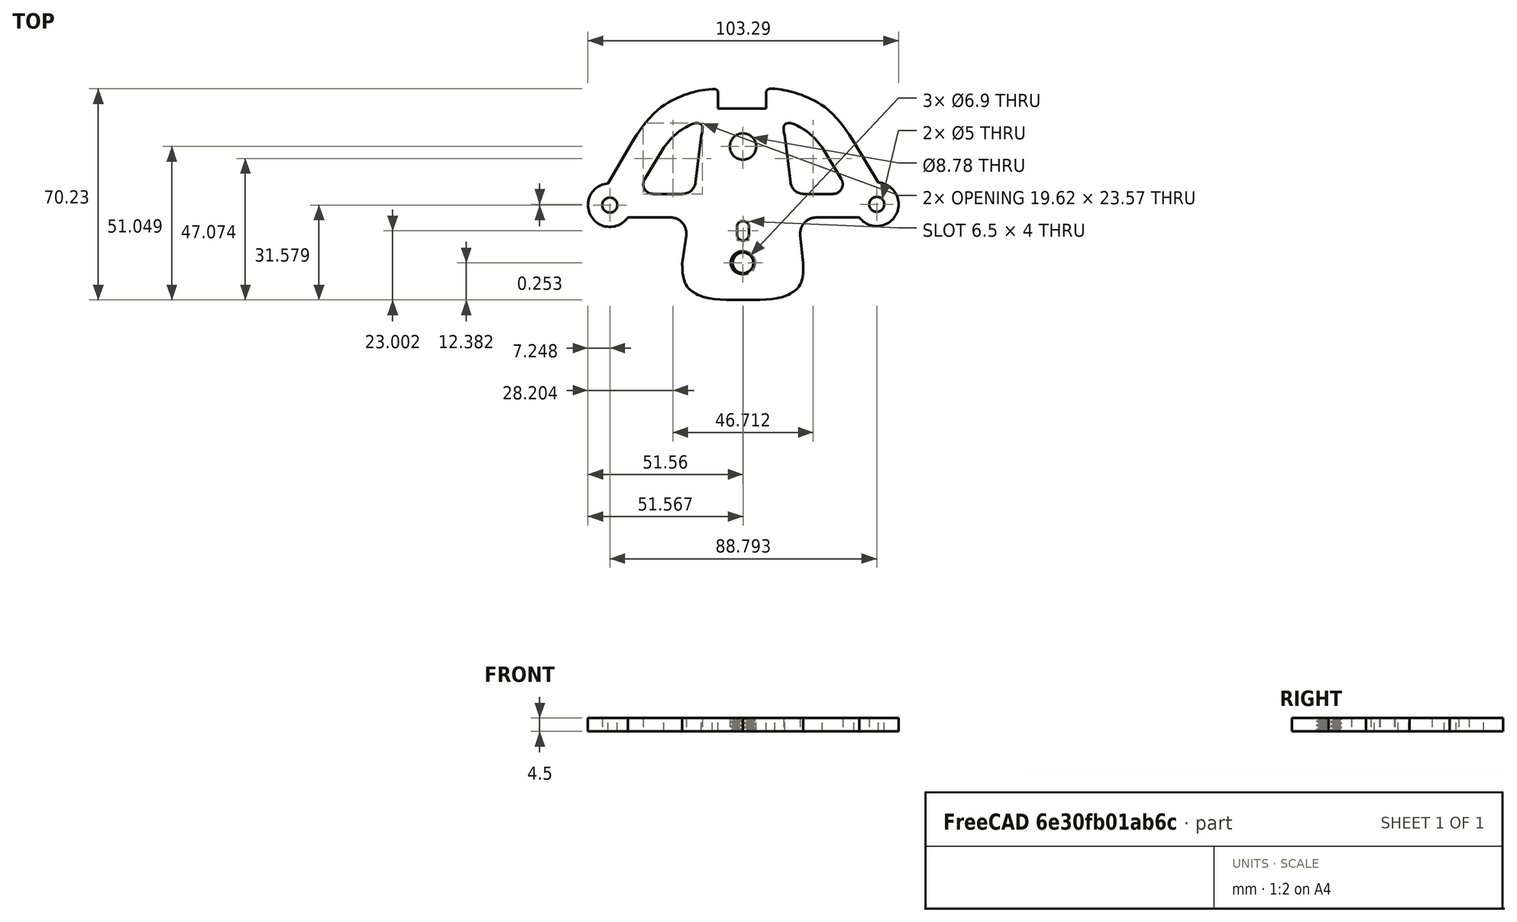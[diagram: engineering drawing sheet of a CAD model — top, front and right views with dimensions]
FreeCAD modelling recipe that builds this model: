
FCSTD DOCUMENT  (FreeCAD 0.20R29603 (Git))
Label: tiller-plate-final-drawing
License: Creative Commons Attribution
LicenseURL: http://creativecommons.org/licenses/by/4.0/
objects: TechDraw::DrawViewDimension×10, TechDraw::DrawRichAnno×4, TechDraw::DrawProjGroupItem×3, Sketcher::SketchObject×2, TechDraw::DrawLeaderLine×2, Image::ImagePlane×1, PartDesign::Pad×1, PartDesign::Hole×1, PartDesign::Body×1, Part::Refine×1, Mesh::Feature×1, TechDraw::DrawSVGTemplate×1, TechDraw::DrawViewPart×1, TechDraw::DrawViewAnnotation×1, TechDraw::DrawProjGroup×1, TechDraw::DrawGeomHatch×1, TechDraw::DrawPage×1
note: 8 computed .brp shape members not serialized (recipe doc carries the construction recipe); baked Part::Feature solids carry a one-line shape summary decoded from their .brp

FEATURE [Image::ImagePlane] ImagePlane
  Placement = pos=(0.718471,-0.887185,-0.1) rot=(0,0,-1;6.26573rad)
  XSize = 116.42
  YSize = 72.9857
FEATURE [Sketcher::SketchObject] Sketch
  FullyConstrained = false
  MapMode = 5
  Support = -> [XY_Plane]
  sketch-geometry (75):
    g0: ArcOfCircle CenterX=-44.3115 CenterY=-4.63128 CenterZ=0 NormalX=0 NormalY=0 NormalZ=1 AngleXU=0 Radius=7.25 StartAngle=1.65486 EndAngle=5.682
    g1: LineSegment StartX=-8.31257 StartY=27.4789 StartZ=0 EndX=7.68743 EndY=27.4789 EndZ=0
    g2: ArcOfCircle CenterX=44.4815 CenterY=-4.37835 CenterZ=0 NormalX=0 NormalY=0 NormalZ=1 AngleXU=0 Radius=7.25 StartAngle=3.79043 EndAngle=7.77353
    g3-g7: Circle x5 (B-spline internal-alignment scaffolding for g8; pole/knot coordinates omitted)
    g8: BSplineCurve PolesCount=5 KnotsCount=3 Degree=3 IsPeriodic=0
    g9: GeomPoint X=-36.8504 Y=16.2655 Z=0
    g10: GeomPoint X=-22.0365 Y=30.9294 Z=0
    g11: GeomPoint X=-10.281 Y=33.9118 Z=0
    g12: LineSegment StartX=-8.31257 StartY=27.4789 StartZ=0 EndX=-8.31257 EndY=32.8031 EndZ=0
    g13: LineSegment StartX=-10.281 StartY=33.9118 StartZ=0 EndX=-9.42128 EndY=33.9118 EndZ=0
    g14: ArcOfCircle CenterX=-9.42128 CenterY=32.8031 CenterZ=0 NormalX=0 NormalY=0 NormalZ=1 AngleXU=0 Radius=1.10871 StartAngle=2.2e-15 EndAngle=1.5708
    g15: LineSegment StartX=-44.9203 StartY=2.59312 StartZ=0 EndX=-36.8504 EndY=16.2655 EndZ=0
    g16: LineSegment StartX=45.0641 StartY=2.84821 StartZ=0 EndX=36.8504 EndY=16.2655 EndZ=0
    g17: BSplineCurve PolesCount=5 KnotsCount=3 Degree=3 IsPeriodic=0
    g18: Circle CenterX=10.5661 CenterY=34.0159 CenterZ=0 NormalX=0 NormalY=0 NormalZ=1 AngleXU=0 Radius=1
    g19: GeomPoint X=10.5661 Y=34.0159 Z=0
    g20: LineSegment StartX=7.68743 StartY=27.4789 StartZ=0 EndX=7.68743 EndY=32.7328 EndZ=0
    g21: LineSegment StartX=10.5661 StartY=34.0159 StartZ=0 EndX=8.9705 EndY=34.0159 EndZ=0
    g22: ArcOfCircle CenterX=8.9705 CenterY=32.7328 CenterZ=0 NormalX=0 NormalY=0 NormalZ=1 AngleXU=0 Radius=1.28307 StartAngle=1.5708 EndAngle=3.14159
    g23: Circle CenterX=0 CenterY=14.839 CenterZ=0 NormalX=0 NormalY=0 NormalZ=1 AngleXU=0 Radius=4.39
    g24: Circle CenterX=-44.3115 CenterY=-4.63128 CenterZ=0 NormalX=0 NormalY=0 NormalZ=1 AngleXU=0 Radius=2.5
    g25: Circle CenterX=44.4815 CenterY=-4.37835 CenterZ=0 NormalX=0 NormalY=0 NormalZ=1 AngleXU=0 Radius=2.5
    g26: Circle CenterX=0 CenterY=-23.8283 CenterZ=0 NormalX=0 NormalY=0 NormalZ=1 AngleXU=0 Radius=3.375
    g27: LineSegment StartX=-24.1418 StartY=-8.73204 StartZ=0 EndX=-38.3327 EndY=-8.73204 EndZ=0
    g28: LineSegment StartX=-18.8831 StartY=-14.7976 StartZ=0 EndX=-20.2109 EndY=-24.0676 EndZ=0
    g29: ArcOfCircle CenterX=-24.1418 CenterY=-14.0444 CenterZ=0 NormalX=0 NormalY=0 NormalZ=1 AngleXU=0 Radius=5.31234 StartAngle=6.14092 EndAngle=7.85398
    g30: LineSegment StartX=24.3717 StartY=-8.75921 StartZ=0 EndX=38.7048 EndY=-8.75921 EndZ=0
    g31: ArcOfCircle CenterX=24.3717 CenterY=-14.1062 CenterZ=0 NormalX=0 NormalY=0 NormalZ=1 AngleXU=0 Radius=5.34701 StartAngle=1.5708 EndAngle=3.24394
    g32: LineSegment StartX=19.0527 StartY=-14.6525 StartZ=0 EndX=20.0104 EndY=-23.9781 EndZ=0
    g33: LineSegment StartX=-1.99308 StartY=-11.9579 StartZ=0 EndX=-1.99308 EndY=-14.4579 EndZ=0
    g34: ArcOfCircle CenterX=0.00691514 CenterY=-14.4579 CenterZ=0 NormalX=0 NormalY=0 NormalZ=1 AngleXU=0 Radius=2 StartAngle=3.14159 EndAngle=6.28319
    g35: LineSegment StartX=2.00692 StartY=-14.4579 StartZ=0 EndX=2.00692 EndY=-11.9579 EndZ=0
    g36: ArcOfCircle CenterX=0.00691514 CenterY=-11.9579 CenterZ=0 NormalX=0 NormalY=0 NormalZ=1 AngleXU=0 Radius=2 StartAngle=0 EndAngle=3.14159
    g37-g41: Circle x5 (B-spline internal-alignment scaffolding for g42; pole/knot coordinates omitted)
    g42: BSplineCurve PolesCount=5 KnotsCount=3 Degree=3 IsPeriodic=0
    g43: GeomPoint X=-20.2109 Y=-24.0676 Z=0
    g44: GeomPoint X=-16.4959 Y=-33.6189 Z=0
    g45: GeomPoint X=0 Y=-36.2033 Z=0
    g46: BSplineCurve PolesCount=5 KnotsCount=3 Degree=3 IsPeriodic=0
    g47: LineSegment StartX=-13.8688 StartY=18.3787 StartZ=0 EndX=-15.7977 EndY=2.95357 EndZ=0
    g48: LineSegment StartX=-29.9555 StartY=-0.921458 StartZ=0 EndX=-20.1874 EndY=-0.921458 EndZ=0
    g49: ArcOfCircle CenterX=-20.1874 CenterY=3.50249 CenterZ=0 NormalX=0 NormalY=0 NormalZ=1 AngleXU=0 Radius=4.42394 StartAngle=4.71239 EndAngle=6.15879
    g50: LineSegment StartX=-26.3153 StartY=14.4759 StartZ=0 EndX=-32.7012 EndY=3.9578 EndZ=0
    g51: ArcOfCircle CenterX=-29.9555 CenterY=2.29074 CenterZ=0 NormalX=0 NormalY=0 NormalZ=1 AngleXU=0 Radius=3.2122 StartAngle=2.59594 EndAngle=4.71239
    g52-g57: Circle x6 (B-spline internal-alignment scaffolding for g58; pole/knot coordinates omitted)
    g58: BSplineCurve PolesCount=6 KnotsCount=4 Degree=3 IsPeriodic=0
    g59-g62: GeomPoint x4 (B-spline internal-alignment scaffolding for g58; pole/knot coordinates omitted)
    g63: GeomPoint X=0 Y=-23.8283 Z=0
    g64: LineSegment StartX=26.3153 StartY=14.4759 StartZ=0 EndX=32.7012 EndY=3.9578 EndZ=0
    g65: BSplineCurve PolesCount=6 KnotsCount=4 Degree=3 IsPeriodic=0
    g66: LineSegment StartX=13.8688 StartY=18.3787 StartZ=0 EndX=15.7977 EndY=2.95357 EndZ=0
    g67: ArcOfCircle CenterX=20.1874 CenterY=3.50249 CenterZ=0 NormalX=0 NormalY=0 NormalZ=1 AngleXU=0 Radius=4.42394 StartAngle=3.26599 EndAngle=4.71239
    g68: LineSegment StartX=29.9555 StartY=-0.921458 StartZ=0 EndX=20.1874 EndY=-0.921458 EndZ=0
    g69: ArcOfCircle CenterX=29.9555 CenterY=2.29074 CenterZ=0 NormalX=0 NormalY=0 NormalZ=1 AngleXU=0 Radius=3.2122 StartAngle=4.71239 EndAngle=6.82884
    g70: GeomPoint X=-0.103427 Y=-16.4548 Z=0
    g71: GeomPoint X=-0.101997 Y=-20.4548 Z=0
    g72: GeomPoint X=0.0131789 Y=-27.2033 Z=0
    g73: GeomPoint X=-0.00257 Y=27.4789 Z=0
    g74: GeomPoint X=-0.0300529 Y=19.2289 Z=0
  constraints (86):
    c: Radius(g0) = 7.25
    c: Horizontal(g1)
    c: Equal(g2,g0)
    c: Equal(g3, g4-g7) x4
    c: InternalAlignment(g3-g7 -> g8) x5
    c: InternalAlignment(g9,g8)
    c: InternalAlignment(g10,g8)
    c: InternalAlignment(g11,g8)
    c: Coincident(g12,g1)
    c: Coincident(g13,g8)
    c: Horizontal(g13)
    c: Tangent(g12,g14) = -1.5708
    c: Tangent(g13,g14) = 1.5708
    c: Coincident(g15,g8)
    c: InternalAlignment(g18,g17)
    c: InternalAlignment(g19,g17)
    c: Coincident(g21,g17)
    c: Horizontal(g21)
    c: Tangent(g20,g22) = 1.5708
    c: Tangent(g21,g22) = -1.5708
    c: Coincident(g16,g17)
    c: PointOnObject(g23,g-2)
    c: Coincident(g24,g0)
    c: Diameter(g24) = 5
    c: Diameter(g25) = 5
    c: PointOnObject(g26,g-2)
    c: Horizontal(g27)
    c: Tangent(g27,g29) = -1.5708
    c: Tangent(g28,g29) = 1.5708
    c: Horizontal(g30)
    c: Tangent(g30,g31) = 1.5708
    c: Tangent(g32,g31) = -1.5708
    c: Coincident(g2,g25)
    c: Vertical(g33)
    c: Tangent(g33,g34) = -1.5708
    c: Tangent(g34,g35) = -1.5708
    c: Tangent(g35,g36) = -1.5708
    c: Radius(g36) = 2
    c: Equal(g34,g36)
    c: DistanceY(g34,g36) = 2.5
    c: Vertical(g35)
    c: Coincident(g33,g36)
    c: Equal(g37, g38-g41) x4
    c: PointOnObject(g42,g-2)
    c: InternalAlignment(g37-g41 -> g42) x5
    c: InternalAlignment(g43,g42)
    c: InternalAlignment(g44,g42)
    c: InternalAlignment(g45,g42)
    c: Coincident(g28,g42)
    c: Horizontal(g48)
    c: Tangent(g47,g49) = 1.5708
    c: Tangent(g48,g49) = -1.5708
    c: Tangent(g48,g51) = -1.5708
    c: Tangent(g50,g51) = -1.5708
    c: Coincident(g58,g50)
    c: Equal(g52, g53-g57) x5
    c: Coincident(g58,g47)
    c: InternalAlignment(g52-g57 -> g58) x6
    c: InternalAlignment(g59-g62 -> g58) x4
    c: Coincident(g63,g26)
    c: Horizontal(g68)
    c: Tangent(g66,g67) = -1.5708
    c: Tangent(g68,g67) = 1.5708
    c: Tangent(g68,g69) = 1.5708
    c: Tangent(g64,g69) = 1.5708
    c: Coincident(g65,g64)
    c: Coincident(g65,g66)
    c: Coincident(g0,g27)
    c: Coincident(g0,g15)
    c: Coincident(g2,g16)
    c: Coincident(g2,g30)
    c: Coincident(g46,g42)
    c: Vertical(g20)
    c: Vertical(g12)
    c: Coincident(g20,g1)
    c: Coincident(g32,g46)
    c: PointOnObject(g70,g34)
    c: PointOnObject(g71,g26)
    c: DistanceY(g71,g70) = 4
    c: PointOnObject(g72,g26)
    c: DistanceY(g42,g72) = 9
    c: PointOnObject(g73,g1)
    c: PointOnObject(g74,g23)
    c: DistanceY(g74,g73) = 8.25
    c: Diameter(g26) = 6.75
    c: Diameter(g23) = 8.78
FEATURE [PartDesign::Pad] Pad  label="Pad-tiller-plate"
  Direction = (0,0,1)
  Length = 4.5
  Length2 = 10
  Profile = -> Sketch
  ReferenceAxis = -> Sketch [N_Axis]
  Refine = true
  Type = 0
FEATURE [Sketcher::SketchObject] Sketch002  label="Sketch-threaded-hole001"
  ExternalGeometry = -> [Pad]
  FullyConstrained = true
  MapMode = 5
  Placement = pos=(0,0,4.5) rot=(0,0,1;0rad)
  Support = -> [Pad]
  sketch-geometry (1):
    g0: Circle CenterX=0 CenterY=-23.8283 CenterZ=0 NormalX=0 NormalY=0 NormalZ=1 AngleXU=0 Radius=3.375
  constraints (2):
    c: Coincident(g0,g-3)
    c: Equal(g0,g-3)
FEATURE [PartDesign::Hole] Hole  label="Hole - tillerPlate with 5/16 threaded UNC"
  BaseFeature = -> Pad
  CustomThreadClearance = 0.3
  Depth = 25
  DepthType = 0
  Diameter = 6.9
  DrillForDepth = false
  DrillPoint = 1
  DrillPointAngle = 118
  HoleCutCountersinkAngle = 90
  HoleCutCustomValues = false
  HoleCutDepth = 0
  HoleCutDiameter = 6.1
  HoleCutType = 0
  ModelThread = true
  Profile = -> Sketch002
  Refine = true
  Tapered = false
  TaperedAngle = 90
  ThreadClass = 0
  ThreadDepth = 25
  ThreadDepthType = 0
  ThreadDirection = 0
  ThreadFit = 0
  ThreadSize = 10
  ThreadType = 3
  Threaded = true
  UseCustomThreadClearance = true
FEATURE [PartDesign::Body] Body  label="Body-tiller-plate"
  Group = -> [Sketch,Pad,Sketch002,Hole]
  Origin = -> Origin
  Tip = -> Hole
FEATURE [Part::Refine] Hole001  label="refined_tillerPlate-with-5/16-UNC-threads"
  Source = -> Hole
FEATURE [Mesh::Feature] Mesh  label="refined_tillerPlate-with-5/16-UNC-threads (Meshed)"
FEATURE [TechDraw::DrawSVGTemplate] Template
  EditableTexts = AUTHOR_NAME=C Greenstreet; DN=CWG1; DRAWING_TITLE=Tiller Plate, Smart Track™ kayak rudder control; FC-DATE=12 Feb 2023; FC-REV=REV 1; FC-SC=2:1; FC-SH=1 / 1; FC-SI=A3; FreeCAD_DRAWING=Email: <email>; PN=n/a; SI-1=Client:  Greg Barbour; SI-2=Mobile:  0 416 871 455; SI-6=FreeCAD DRAWING
  Height = 297
  Orientation = 1
  Width = 420
FEATURE [TechDraw::DrawProjGroupItem] ProjItem  label="Front"
  CoarseView = false
  Direction = (0,0,1)
  Focus = 100
  HardHidden = false
  IsoCount = 0
  IsoHidden = false
  IsoVisible = false
  LockPosition = true
  Perspective = false
  Rotation = 0
  RotationVector = (-1,0,0)
  Scale = 2
  ScaleType = 2
  SeamHidden = false
  SeamVisible = true
  SmoothHidden = false
  SmoothVisible = true
  Source = -> [Hole001]
  Type = 0
  X = 0
  XDirection = (-1,0,0)
  Y = 0
FEATURE [TechDraw::DrawProjGroupItem] ProjItem001  label="Bottom"
  CoarseView = false
  Direction = (0,1,0)
  Focus = 100
  HardHidden = false
  IsoCount = 0
  IsoHidden = false
  IsoVisible = false
  LockPosition = true
  Perspective = false
  Rotation = 0
  RotationVector = (1,0,0)
  ScaleType = 2
  SeamHidden = false
  SeamVisible = true
  SmoothHidden = false
  SmoothVisible = true
  Source = -> [Hole001]
  Type = 5
  X = 0
  XDirection = (-1,0,0)
  Y = 122.244
FEATURE [TechDraw::DrawViewPart] View001  label="Isometric"
  CoarseView = false
  Direction = (-0.418,0.525,0.741)
  Focus = 100
  HardHidden = false
  IsoCount = 0
  IsoHidden = false
  IsoVisible = false
  LockPosition = false
  Perspective = false
  Rotation = 0
  Scale = 1.5
  ScaleType = 2
  SeamHidden = false
  SeamVisible = true
  SmoothHidden = false
  SmoothVisible = true
  Source = -> [Hole001]
  X = 333.972
  XDirection = (-0.908,-0.253,-0.334)
  Y = 229.841
FEATURE [TechDraw::DrawViewDimension] Dimension001
  AngleOverride = false
  Arbitrary = false
  ArbitraryTolerances = false
  EqualTolerance = true
  ExtensionAngle = 0
  FormatSpec = ⌀%.2w
  FormatSpecOverTolerance = %+.2w
  FormatSpecUnderTolerance = %+.2w
  Inverted = false
  LineAngle = 0
  LockPosition = false
  MeasureType = 1
  OverTolerance = 0
  References2D = -> [ProjItem]
  Rotation = 0
  ScaleType = 0
  TheoreticalExact = false
  Type = 5
  UnderTolerance = 0
  X = 70.009
  Y = 12.5016
FEATURE [TechDraw::DrawViewDimension] Dimension002
  AngleOverride = false
  Arbitrary = false
  ArbitraryTolerances = false
  EqualTolerance = true
  ExtensionAngle = 0
  FormatSpec = ⌀%.2w
  FormatSpecOverTolerance = %+.2w
  FormatSpecUnderTolerance = %+.2w
  Inverted = false
  LineAngle = 0
  LockPosition = false
  MeasureType = 1
  OverTolerance = 0
  References2D = -> [ProjItem]
  Rotation = 0
  ScaleType = 0
  TheoreticalExact = false
  Type = 5
  UnderTolerance = 0
  X = -15.627
  Y = -13.1267
FEATURE [TechDraw::DrawViewDimension] Dimension003
  AngleOverride = false
  Arbitrary = false
  ArbitraryTolerances = false
  EqualTolerance = true
  ExtensionAngle = 0
  FormatSpec = R%.2w
  FormatSpecOverTolerance = %+.2w
  FormatSpecUnderTolerance = %+.2w
  Inverted = false
  LineAngle = 0
  LockPosition = false
  MeasureType = 1
  OverTolerance = 0
  References2D = -> [ProjItem]
  Rotation = 0
  ScaleType = 0
  TheoreticalExact = false
  Type = 4
  UnderTolerance = 0
  X = 9.62955
  Y = 37.8902
FEATURE [TechDraw::DrawViewDimension] Dimension004
  AngleOverride = false
  Arbitrary = false
  ArbitraryTolerances = false
  EqualTolerance = true
  ExtensionAngle = 0
  FormatSpec = %.2w
  FormatSpecOverTolerance = %+.2w
  FormatSpecUnderTolerance = %+.2w
  Inverted = false
  LineAngle = 0
  LockPosition = false
  MeasureType = 1
  OverTolerance = 0
  References2D = -> [ProjItem]
  Rotation = 0
  ScaleType = 0
  TheoreticalExact = false
  Type = 2
  UnderTolerance = 0
  X = -10.7296
  Y = 28.37
FEATURE [TechDraw::DrawViewDimension] Dimension005
  AngleOverride = false
  Arbitrary = false
  ArbitraryTolerances = false
  EqualTolerance = true
  ExtensionAngle = 0
  FormatSpec = R%.2w
  FormatSpecOverTolerance = %+.2w
  FormatSpecUnderTolerance = %+.2w
  Inverted = false
  LineAngle = 0
  LockPosition = false
  MeasureType = 1
  OverTolerance = 0
  References2D = -> [ProjItem]
  Rotation = 0
  ScaleType = 0
  TheoreticalExact = false
  Type = 4
  UnderTolerance = 0
  X = 15.7004
  Y = 25.3299
FEATURE [TechDraw::DrawViewAnnotation] Annotation
  Font = osifont
  LineSpace = 80
  LockPosition = false
  MaxWidth = -1
  Rotation = 0
  ScaleType = 0
  Text = Drawing not fully dimensioned | Refer to digital DXF file for cutting | Dimensions in mm unless annotated differently | Holes unthreaded unless specified | Recommended Material: AISA 304 (marine grade) 4.5 mm stainless steel plate or similar
  TextSize = 5
  TextStyle = 0
  X = 115.536
  Y = 37.9241
FEATURE [TechDraw::DrawLeaderLine] LeaderLine
  AutoHorizontal = true
  EndSymbol = 7
  LeaderParent = -> ProjItem
  LockPosition = true
  Rotation = 0
  Scalable = false
  ScaleType = 0
  StartSymbol = 0
  WayPoints = (3) [(0,0,0),(-229.415,-303.82,0),(-93.0063,-303.82,0)]
  X = -0.342471
  Y = 27.1711
FEATURE [TechDraw::DrawRichAnno] RichTextAnnotation
  AnnoText = <!DOCTYPE HTML PUBLIC "-//W3C//DTD HTML 4.0//EN" "http://www.w3.org/TR/REC-html40/strict.dtd">\n<html><head><meta name="qrichtext" content="1" /><style type="text/css">\np, li { white-space: pre-wrap; }\n</style></head><body style=" font-family:'osifont'; font-size:9pt; font-weight:400; font-style:normal;">\n<p style=" margin-top:0px; margin-bottom:0px; margin-left:0px; margin-right:0px; -qt-block-indent:0; text-indent:0px;"><span style=" font-size:16pt; font-weight:600;"> </span><span style=" font-size:16pt;">5/16 inch UNC threaded hole</span></p>\n<p style=" margin-top:0px; margin-bottom:0px; margin-left:0px; margin-right:0px; -qt-block-indent:0; text-indent:0px;"><span style=" font-size:12pt;">  (17/64 inch or 6.75 mm tap hole size)</span></p></body></html>
  LockPosition = false
  MaxWidth = -1
  Rotation = 0
  ScaleType = 0
  ShowFrame = false
  X = 165.255
  Y = 238.664
FEATURE [TechDraw::DrawViewDimension] Dimension007
  AngleOverride = false
  Arbitrary = false
  ArbitraryTolerances = false
  EqualTolerance = true
  ExtensionAngle = 0
  FormatSpec = %.2w
  FormatSpecOverTolerance = %+.2w
  FormatSpecUnderTolerance = %+.2w
  Inverted = false
  LineAngle = 0
  LockPosition = false
  MeasureType = 1
  OverTolerance = 0
  References2D = -> [ProjItem]
  Rotation = 0
  ScaleType = 0
  TheoreticalExact = false
  Type = 1
  UnderTolerance = 0
  X = 0.817493
  Y = -58.6857
FEATURE [TechDraw::DrawViewDimension] Dimension008
  AngleOverride = false
  Arbitrary = false
  ArbitraryTolerances = false
  EqualTolerance = true
  ExtensionAngle = 0
  FormatSpec = %.2w
  FormatSpecOverTolerance = %+.2w
  FormatSpecUnderTolerance = %+.2w
  Inverted = false
  LineAngle = 0
  LockPosition = false
  MeasureType = 1
  OverTolerance = 0
  References2D = -> [ProjItem001]
  Rotation = 0
  ScaleType = 0
  TheoreticalExact = false
  Type = 1
  UnderTolerance = 0
  X = 1.27804
  Y = -7.82423
FEATURE [TechDraw::DrawProjGroupItem] ProjItem002  label="Left"
  CoarseView = false
  Direction = (1,0,1e-16)
  Focus = 100
  HardHidden = false
  IsoCount = 0
  IsoHidden = false
  IsoVisible = false
  LockPosition = true
  Perspective = false
  Rotation = 0
  RotationVector = (1,0,0)
  ScaleType = 2
  SeamHidden = false
  SeamVisible = true
  SmoothHidden = false
  SmoothVisible = true
  Source = -> [Hole001]
  Type = 1
  X = 117.484
  XDirection = (-1e-16,0,1)
  Y = 0
FEATURE [TechDraw::DrawProjGroup] ProjGroup
  Anchor = -> ProjItem
  AutoDistribute = true
  LockPosition = false
  ProjectionType = 0
  Rotation = 0
  Scale = 2
  ScaleType = 2
  Source = -> [Hole001]
  Views = -> [ProjItem,ProjItem001,ProjItem002]
  X = 126.475
  Y = 151.754
  spacingX = 15
  spacingY = 0
FEATURE [TechDraw::DrawViewDimension] Dimension009
  AngleOverride = false
  Arbitrary = false
  ArbitraryTolerances = false
  EqualTolerance = true
  ExtensionAngle = 0
  FormatSpec = %.2w
  FormatSpecOverTolerance = %+.2w
  FormatSpecUnderTolerance = %+.2w
  Inverted = false
  LineAngle = 0
  LockPosition = false
  MeasureType = 1
  OverTolerance = 0
  References2D = -> [ProjItem002]
  Rotation = 0
  ScaleType = 0
  TheoreticalExact = false
  Type = 2
  UnderTolerance = 0
  X = 10.5685
  Y = 10.1948
FEATURE [TechDraw::DrawViewDimension] Dimension011
  AngleOverride = false
  Arbitrary = false
  ArbitraryTolerances = false
  EqualTolerance = true
  ExtensionAngle = 0
  FormatSpec = R%.2w
  FormatSpecOverTolerance = %+.2w
  FormatSpecUnderTolerance = %+.2w
  Inverted = false
  LineAngle = 0
  LockPosition = false
  MeasureType = 1
  OverTolerance = 0
  References2D = -> [ProjItem]
  Rotation = 0
  ScaleType = 0
  TheoreticalExact = false
  Type = 4
  UnderTolerance = 0
  X = -74.7147
  Y = 37.6713
FEATURE [TechDraw::DrawGeomHatch] GeomHatch  label="GeomHatchFX1"
  FilePattern = <path>
  NamePattern = Diamond
  ScalePattern = 1
  Source = -> View001 [Face1]
FEATURE [TechDraw::DrawRichAnno] RichTextAnnotation001
  AnnoText = <!DOCTYPE HTML PUBLIC "-//W3C//DTD HTML 4.0//EN" "http://www.w3.org/TR/REC-html40/strict.dtd">\n<html><head><meta name="qrichtext" content="1" /><style type="text/css">\np, li { white-space: pre-wrap; }\n</style></head><body style=" font-family:'osifont'; font-size:9pt; font-weight:400; font-style:normal;">\n<p style=" margin-top:0px; margin-bottom:0px; margin-left:0px; margin-right:0px; -qt-block-indent:0; text-indent:0px;"><span style=" font-size:12pt; font-style:italic;">Any sharp edges bevelled/smoothed</span></p></body></html>
  LockPosition = false
  MaxWidth = -1
  Rotation = 0
  ScaleType = 0
  ShowFrame = false
  X = 83.9414
  Y = 101.919
FEATURE [TechDraw::DrawLeaderLine] LeaderLine001
  AutoHorizontal = true
  EndSymbol = 7
  LeaderParent = -> ProjItem
  LockPosition = true
  Rotation = 0
  Scalable = false
  ScaleType = 0
  StartSymbol = 0
  WayPoints = (3) [(0,0,0),(-177.365,333.688,0),(-42.0867,333.688,0)]
  X = -42.6452
  Y = -9.44001
FEATURE [TechDraw::DrawRichAnno] RichTextAnnotation002
  AnnoText = <!DOCTYPE HTML PUBLIC "-//W3C//DTD HTML 4.0//EN" "http://www.w3.org/TR/REC-html40/strict.dtd">\n<html><head><meta name="qrichtext" content="1" /><style type="text/css">\np, li { white-space: pre-wrap; }\n</style></head><body style=" font-family:'osifont'; font-size:9pt; font-weight:400; font-style:normal;">\n<p style=" margin-top:0px; margin-bottom:0px; margin-left:0px; margin-right:0px; -qt-block-indent:0; text-indent:0px;"><span style=" font-size:36pt;">Top View</span></p></body></html>
  LockPosition = false
  MaxWidth = -1
  Rotation = 0
  ScaleType = 0
  ShowFrame = false
  X = 55.4056
  Y = 227.667
FEATURE [TechDraw::DrawRichAnno] RichTextAnnotation003
  AnnoParent = -> RichTextAnnotation002
  AnnoText = <!DOCTYPE HTML PUBLIC "-//W3C//DTD HTML 4.0//EN" "http://www.w3.org/TR/REC-html40/strict.dtd">\n<html><head><meta name="qrichtext" content="1" /><style type="text/css">\np, li { white-space: pre-wrap; }\n</style></head><body style=" font-family:'osifont'; font-size:9pt; font-weight:400; font-style:normal;">\n<p style=" margin-top:0px; margin-bottom:0px; margin-left:0px; margin-right:0px; -qt-block-indent:0; text-indent:0px;"><span style=" font-size:36pt;">Isometric View</span></p></body></html>
  LockPosition = false
  MaxWidth = -1
  Rotation = 0
  ScaleType = 0
  ShowFrame = false
  X = 273.657
  Y = -57.3495
FEATURE [TechDraw::DrawViewDimension] Dimension012
  AngleOverride = false
  Arbitrary = false
  ArbitraryTolerances = false
  EqualTolerance = true
  ExtensionAngle = 0
  FormatSpec = %.2w
  FormatSpecOverTolerance = %+.2w
  FormatSpecUnderTolerance = %+.2w
  Inverted = false
  LineAngle = 0
  LockPosition = false
  MeasureType = 1
  OverTolerance = 0
  References2D = -> [ProjItem]
  Rotation = 0
  ScaleType = 0
  TheoreticalExact = false
  Type = 2
  UnderTolerance = 0
  X = 21.5336
  Y = -59.9691
FEATURE [TechDraw::DrawPage] Page  label="Tech-drawing"
  KeepUpdated = true
  NextBalloonIndex = 1
  ProjectionType = 0
  Template = -> Template
  Views = -> [ProjGroup,View001,Dimension001,Dimension002,Dimension003,Dimension004,Dimension005,Annotation,LeaderLine,RichTextAnnotation,Dimension007,Dimension008,Dimension009,Dimension011,RichTextAnnotation001,LeaderLine001,RichTextAnnotation002,RichTextAnnotation003,Dimension012]
note: 1 file-system path scrubbed to <path> (originals preserved in the JSON sidecar)
